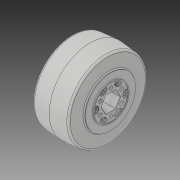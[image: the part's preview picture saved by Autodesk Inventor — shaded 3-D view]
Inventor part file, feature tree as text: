
AUTODESK INVENTOR PART (.ipt)
format: ipt  version: 2019 (Build 230136000, 136)  size: 1,171,456 bytes
history: native  units: in
note: dims shown in document units (in); Inventor stores cm internally (conversion verified against a paired STEP export)
features: revolve x1
ambient origin geometry x8: Origin, YZ Plane, XZ Plane, XY Plane, X Axis, Y Axis, Z Axis, Center Point
bodies: Solid1 (feature_tree)
feature tree (1):
  revolve  "Revolve1"  [1 undecoded]
note: 1 required parameter value undecoded (feature->parameter linkage not recoverable at this tier; creation-order binding heuristic only, values carry confidence <= 0.55)
